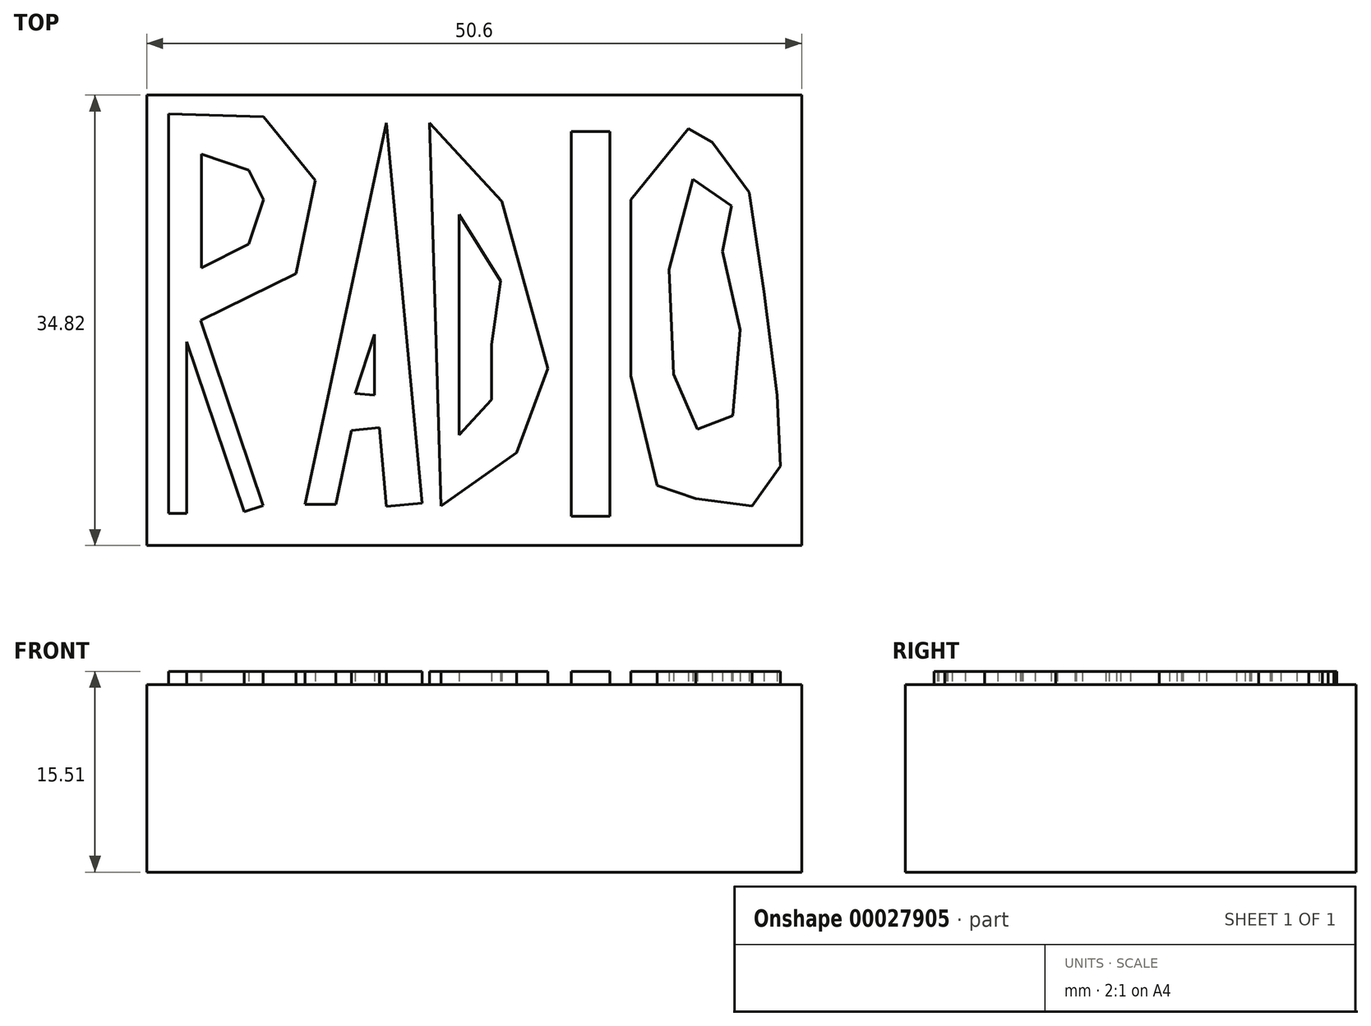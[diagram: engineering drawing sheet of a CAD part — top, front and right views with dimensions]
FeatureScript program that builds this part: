
annotation { "Feature Type Name" : "Feature", "Feature Type Description" : "" }
export const myFeature = defineFeature(function(context is Context, id is Id, definition is map)
    precondition{}
    {
        {
            var Q0;
            Q0=qCreatedBy(makeId("Top.planeOp"),FACE);
            var sketch = newSketch(context, id + "F0", { "sketchPlane" : qUnion([Q0])});
            skLineSegment(sketch, "E0.rect.bottom", {"start": v(25.3, 17.42) * mm, "end": v(-25.3, 17.42) * mm});
            skLineSegment(sketch, "E0.rect.top", {"start": v(25.3, -17.42) * mm, "end": v(-25.3, -17.42) * mm});
            skLineSegment(sketch, "E0.rect.left", {"start": v(25.3, 17.42) * mm, "end": v(25.3, -17.42) * mm});
            skLineSegment(sketch, "E0.rect.right", {"start": v(-25.3, 17.42) * mm, "end": v(-25.3, -17.42) * mm});
            skPoint(sketch, "E0.rect.middle", {"position": v(0, 0) * mm});
            skSolve(sketch);
        }
        {
            var Q0;
            Q0 = qSketchRegion(id + "F0", true);
            extrude(context, id + "F1", {"entities" : qUnion([Q0]), "depth" : 14.5 * mm});
        }
        {
            var Q0;
            Q0=makeQuery(id+"F1.opExtrude","CAP_FACE",FACE,{"disambiguationData":[OSD([sQuery(id+"F0.wireOp",EDGE,"E0.rect.bottom"),sQuery(id+"F0.wireOp",EDGE,"E0.rect.top"),sQuery(id+"F0.wireOp",EDGE,"E0.rect.left"),sQuery(id+"F0.wireOp",EDGE,"E0.rect.right")])],"isStart":false});
            var sketch = newSketch(context, id + "F2", { "sketchPlane" : qUnion([Q0])});
            skLineSegment(sketch, "E1", {"start": v(-23.6, 15.95) * mm, "end": v(-23.6, -14.93) * mm});
            skLineSegment(sketch, "E2", {"start": v(-23.6, -14.93) * mm, "end": v(-22.23, -14.93) * mm});
            skLineSegment(sketch, "E3", {"start": v(-22.23, -14.93) * mm, "end": v(-22.23, -1.66) * mm});
            skLineSegment(sketch, "E4", {"start": v(-22.23, -1.66) * mm, "end": v(-17.77, -14.82) * mm});
            skLineSegment(sketch, "E5", {"start": v(-17.77, -14.82) * mm, "end": v(-16.3, -14.32) * mm});
            skLineSegment(sketch, "E6", {"start": v(-16.3, -14.32) * mm, "end": v(-21.16, 0) * mm});
            skLineSegment(sketch, "E7", {"start": v(-21.16, 0) * mm, "end": v(-13.77, 3.6) * mm});
            skLineSegment(sketch, "E8", {"start": v(-13.77, 3.6) * mm, "end": v(-12.28, 10.8) * mm});
            skLineSegment(sketch, "E9", {"start": v(-12.28, 10.8) * mm, "end": v(-16.28, 15.72) * mm});
            skLineSegment(sketch, "E10", {"start": v(-16.28, 15.72) * mm, "end": v(-23.6, 15.95) * mm});
            skLineSegment(sketch, "E11", {"start": v(-21.09, 12.86) * mm, "end": v(-21.09, 4.06) * mm});
            skLineSegment(sketch, "E12", {"start": v(-21.09, 4.06) * mm, "end": v(-17.43, 5.89) * mm});
            skLineSegment(sketch, "E13", {"start": v(-17.43, 5.89) * mm, "end": v(-16.28, 9.32) * mm});
            skLineSegment(sketch, "E14", {"start": v(-16.28, 9.32) * mm, "end": v(-17.43, 11.6) * mm});
            skLineSegment(sketch, "E15", {"start": v(-17.43, 11.6) * mm, "end": v(-21.09, 12.86) * mm});
            skLineSegment(sketch, "E16", {"start": v(-13.08, -14.25) * mm, "end": v(-6.79, 15.27) * mm});
            skLineSegment(sketch, "E17", {"start": v(-6.79, 15.27) * mm, "end": v(-4.04, -14.13) * mm});
            skLineSegment(sketch, "E18", {"start": v(-4.04, -14.13) * mm, "end": v(-6.78, -14.39) * mm});
            skLineSegment(sketch, "E19", {"start": v(-6.78, -14.39) * mm, "end": v(-7.34, -8.3) * mm});
            skLineSegment(sketch, "E20", {"start": v(-7.34, -8.3) * mm, "end": v(-9.48, -8.5) * mm});
            skLineSegment(sketch, "E21", {"start": v(-9.48, -8.5) * mm, "end": v(-10.7, -14.25) * mm});
            skLineSegment(sketch, "E22", {"start": v(-10.7, -14.25) * mm, "end": v(-13.08, -14.25) * mm});
            skLineSegment(sketch, "E23", {"start": v(-9.2, -5.67) * mm, "end": v(-7.7, -1.1) * mm});
            skLineSegment(sketch, "E24", {"start": v(-7.7, -1.1) * mm, "end": v(-7.7, -5.78) * mm});
            skLineSegment(sketch, "E25", {"start": v(-7.7, -5.78) * mm, "end": v(-9.2, -5.67) * mm});
            skLineSegment(sketch, "E26", {"start": v(-3.47, 15.27) * mm, "end": v(-2.56, -14.36) * mm});
            skLineSegment(sketch, "E27", {"start": v(-2.56, -14.36) * mm, "end": v(3.28, -10.24) * mm});
            skLineSegment(sketch, "E28", {"start": v(3.28, -10.24) * mm, "end": v(5.68, -3.72) * mm});
            skLineSegment(sketch, "E29", {"start": v(5.68, -3.72) * mm, "end": v(2.13, 9.2) * mm});
            skLineSegment(sketch, "E30", {"start": v(2.13, 9.2) * mm, "end": v(-3.47, 15.27) * mm});
            skLineSegment(sketch, "E31", {"start": v(-1.18, 8.17) * mm, "end": v(-1.18, -8.87) * mm});
            skLineSegment(sketch, "E32", {"start": v(-1.18, -8.87) * mm, "end": v(1.33, -6.13) * mm});
            skLineSegment(sketch, "E33", {"start": v(1.33, -6.13) * mm, "end": v(1.33, -1.9) * mm});
            skLineSegment(sketch, "E34", {"start": v(1.33, -1.9) * mm, "end": v(2.02, 3.03) * mm});
            skLineSegment(sketch, "E35", {"start": v(-1.18, 8.17) * mm, "end": v(2.02, 3.03) * mm});
            skLineSegment(sketch, "E36", {"start": v(7.51, 14.58) * mm, "end": v(7.51, -15.16) * mm});
            skLineSegment(sketch, "E37", {"start": v(7.51, -15.16) * mm, "end": v(10.48, -15.16) * mm});
            skLineSegment(sketch, "E38", {"start": v(10.48, -15.16) * mm, "end": v(10.48, 14.58) * mm});
            skLineSegment(sketch, "E39", {"start": v(10.48, 14.58) * mm, "end": v(7.51, 14.58) * mm});
            skLineSegment(sketch, "E40", {"start": v(16.55, 14.8) * mm, "end": v(12.09, 9.32) * mm});
            skLineSegment(sketch, "E41", {"start": v(12.09, 9.32) * mm, "end": v(12.09, -4.3) * mm});
            skLineSegment(sketch, "E42", {"start": v(12.09, -4.3) * mm, "end": v(14.15, -12.76) * mm});
            skLineSegment(sketch, "E43", {"start": v(14.15, -12.76) * mm, "end": v(17.12, -13.8) * mm});
            skLineSegment(sketch, "E44", {"start": v(17.12, -13.8) * mm, "end": v(21.47, -14.36) * mm});
            skLineSegment(sketch, "E45", {"start": v(21.47, -14.36) * mm, "end": v(23.64, -11.27) * mm});
            skLineSegment(sketch, "E46", {"start": v(23.64, -11.27) * mm, "end": v(23.41, -5.78) * mm});
            skLineSegment(sketch, "E47", {"start": v(23.41, -5.78) * mm, "end": v(22.38, 2.23) * mm});
            skLineSegment(sketch, "E48", {"start": v(22.38, 2.23) * mm, "end": v(21.24, 9.89) * mm});
            skLineSegment(sketch, "E49", {"start": v(21.24, 9.89) * mm, "end": v(18.38, 13.78) * mm});
            skLineSegment(sketch, "E50", {"start": v(18.38, 13.78) * mm, "end": v(16.55, 14.8) * mm});
            skLineSegment(sketch, "E51", {"start": v(16.9, 10.92) * mm, "end": v(15.06, 3.94) * mm});
            skLineSegment(sketch, "E52", {"start": v(15.06, 3.94) * mm, "end": v(15.4, -4.18) * mm});
            skLineSegment(sketch, "E53", {"start": v(15.4, -4.18) * mm, "end": v(17.23, -8.41) * mm});
            skLineSegment(sketch, "E54", {"start": v(17.23, -8.41) * mm, "end": v(19.98, -7.38) * mm});
            skLineSegment(sketch, "E55", {"start": v(19.98, -7.38) * mm, "end": v(20.55, -0.75) * mm});
            skLineSegment(sketch, "E56", {"start": v(20.55, -0.75) * mm, "end": v(19.18, 5.31) * mm});
            skLineSegment(sketch, "E57", {"start": v(19.18, 5.31) * mm, "end": v(19.87, 8.86) * mm});
            skLineSegment(sketch, "E58", {"start": v(19.87, 8.86) * mm, "end": v(16.9, 10.92) * mm});
            skSolve(sketch);
        }
        {
            var Q0;
            Q0 = qSketchRegion(id + "F2", true);
            extrude(context, id + "F3", {"entities" : qUnion([Q0]), "operationType" : NewBodyOperationType.ADD, "depth" : 1 * mm});
        }
    });
